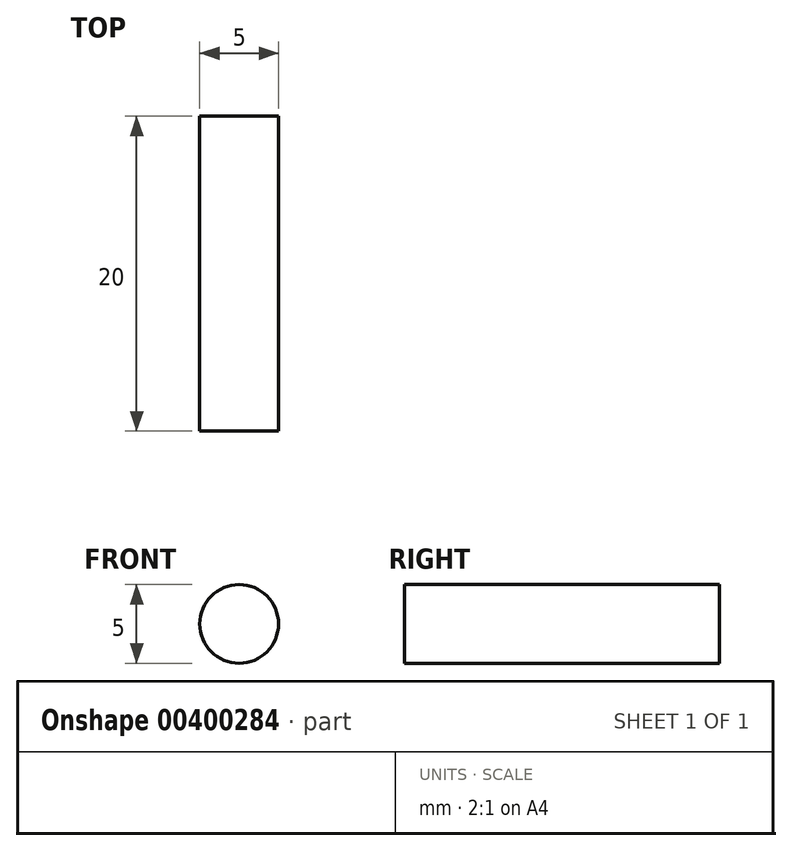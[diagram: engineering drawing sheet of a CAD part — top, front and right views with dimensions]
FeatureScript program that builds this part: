
annotation { "Feature Type Name" : "Feature", "Feature Type Description" : "" }
export const myFeature = defineFeature(function(context is Context, id is Id, definition is map)
    precondition{}
    {
        {
            var Q0;
            Q0=qCreatedBy(makeId("Front.planeOp"),FACE);
            var sketch = newSketch(context, id + "F0", { "sketchPlane" : qUnion([Q0])});
            skCircle(sketch, "E0", {"center": v(0, 0) * mm, "radius": 2.5 * mm});
            skSolve(sketch);
        }
        {
            var Q0;
            Q0 = qSketchRegion(id + "F0", true);
            extrude(context, id + "F1", {"entities" : qUnion([Q0]), "depth" : 20 * mm});
        }
    });
